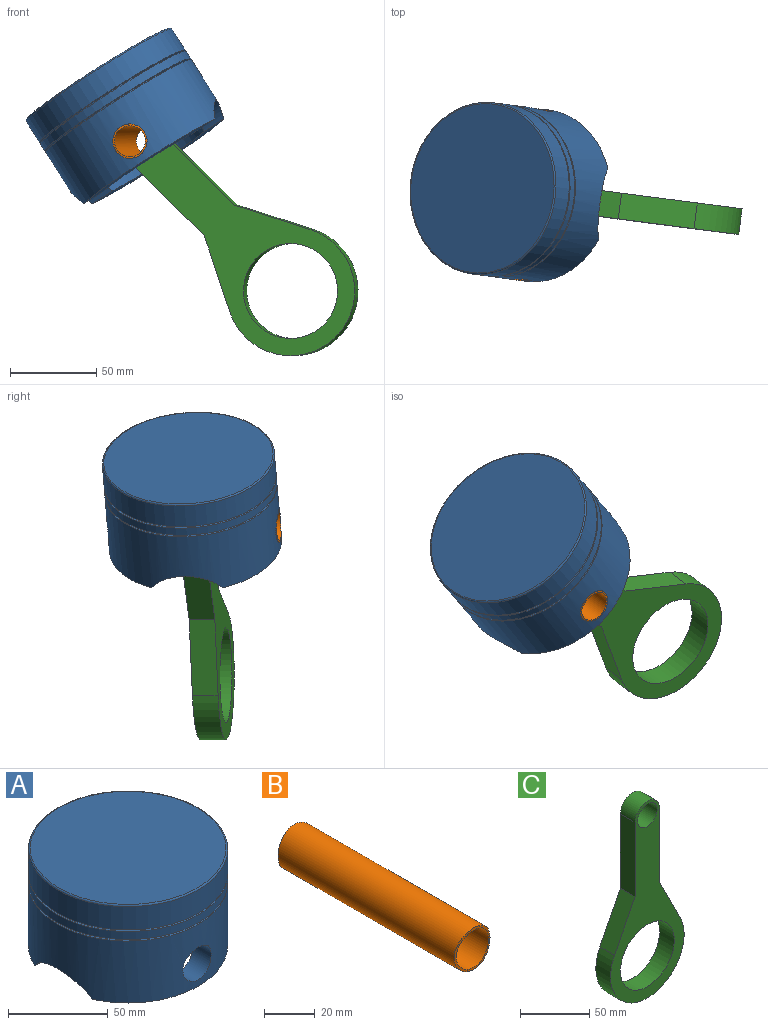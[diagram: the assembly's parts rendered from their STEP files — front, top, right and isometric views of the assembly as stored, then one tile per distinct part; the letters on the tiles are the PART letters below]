
ASSEMBLY  parts=3 mates=2
PART A: 21 faces, bbox 108.2x108.2x60 mm
  f0: plane 91.18x29.47mm, normal (0,0,-1), area 1174.4mm2, adj f10,f12,f17,f18
  f1: plane 98.36x98.36mm, normal (0,0,1), area 7598.2mm2, adj f20
  f2: cylinder r=50mm len=100mm, axis (0,0,-1), area 4498.8mm2, adj f3,f20
  f3: plane 100x100mm, normal (0,0,-1), area 1742.2mm2, adj f2,f4
  f4: cylinder r=44.11mm len=88.21mm, axis (0,0,-1), area 261.3mm2, adj f3,f5
  f5: plane 100x100mm, normal (0,0,1), area 1742.2mm2, adj f4,f6
  f6: cylinder r=50mm len=100mm, axis (0,0,-1), area 1550.4mm2, adj f5,f7
  f7: plane 100x100mm, normal (0,0,-1), area 1742.2mm2, adj f6,f8
  f8: cylinder r=44.11mm len=88.21mm, axis (0,0,-1), area 261.3mm2, adj f7,f9
  f9: plane 100x100mm, normal (0,0,1), area 1742.2mm2, adj f8,f10
  f10: cylinder r=50mm len=100mm, axis (0,0,-1), area 10688.4mm2, adj f0,f9,f11,f14,f15,f16,f17,f18
  f11: plane 91.18x29.47mm, normal (0,0,-1), area 1174.4mm2, adj f10,f12,f16,f19
  f12: cylinder r=37.62mm len=75.24mm, axis (0,0,-1), area 9955mm2, adj f0,f11,f13,f14,f15,f16,f17,f18
  f13: plane 75.24x75.24mm, normal (0,0,-1), area 4446.1mm2, adj f12
  f14: cylinder r=10mm len=20mm, axis (0,-1,0), area 788.7mm2, adj f10,f12
  f15: cylinder r=10mm len=20mm, axis (0,-1,0), area 788.5mm2, adj f10,f12
  f16: cylinder r=25.38mm len=20.53mm, axis (1,0,0), area 312.2mm2, adj f10,f11,f12,f17
  f17: cylinder r=25.38mm len=20.53mm, axis (1,0,0), area 312.2mm2, adj f0,f10,f12,f16
  f18: cylinder r=25.38mm len=20.53mm, axis (1,0,0), area 312.2mm2, adj f0,f10,f12,f19
  f19: cylinder r=25.38mm len=20.53mm, axis (1,0,0), area 312.2mm2, adj f10,f11,f12,f18
  f20: torus R=49.18mm, axis (0,0,-1), area 402.6mm2, adj f1,f2
PART B: 7 faces, bbox 20x99.9x20 mm
  f0: plane 6.99x1.71mm, normal (0,-1,0), area 7.2mm2, adj f1,f2,f4,f5
  f1: cylinder r=9mm len=99.88mm, axis (0,1,0), area 5607.7mm2, adj f0,f3,f4,f5,f6
  f2: cylinder r=10mm len=99.88mm, axis (0,1,0), area 6218.8mm2, adj f0,f3,f4,f5,f6
  f3: plane 6.99x1.71mm, normal (0,-1,0), area 7.2mm2, adj f1,f2,f4,f5
  f4: cylinder r=50mm len=18.74mm, axis (0,0,-1), area 23mm2, adj f0,f1,f2,f3
  f5: cylinder r=50mm len=18.74mm, axis (0,0,-1), area 23mm2, adj f0,f1,f2,f3
  f6: cylinder r=50mm len=20mm, axis (0,0,-1), area 60.2mm2, adj f1,f2
PART C: 10 faces, bbox 75x15x173.9 mm
  f0: cylinder r=12.5mm len=25mm, axis (0,1,0), area 589mm2, adj f1,f5,f8,f9
  f1: plane 65.55x15mm, normal (-1,0,0), area 983.3mm2, adj f0,f2,f8,f9
  f2: plane 41.4x20.96mm, normal (-0.89,0,0.45), area 696.1mm2, adj f1,f3,f8,f9
  f3: cylinder r=37.5mm len=75mm, axis (0,1,0), area 2294.3mm2, adj f2,f4,f8,f9
  f4: plane 41.4x20.96mm, normal (0.89,0,0.45), area 696.1mm2, adj f3,f5,f8,f9
  f5: plane 65.55x15mm, normal (1,0,0), area 983.3mm2, adj f0,f4,f8,f9
  f6: cylinder r=10mm len=20mm, axis (0,1,0), area 942.5mm2, adj f8,f9
  f7: cylinder r=27.5mm len=55mm, axis (0,1,0), area 2591.8mm2, adj f8,f9
  f8: plane 173.89x75mm, normal (0,-1,0), area 4531.6mm2, adj f0,f1,f2,f3,f4,f5,f6,f7
  f9: plane 173.89x75mm, normal (0,1,0), area 4531.6mm2, adj f0,f1,f2,f3,f4,f5,f6,f7
PLACE A rot(axis=(-0.28,0.02,0.96),173deg) t=(-153.11,-41.99,-285.9)mm
PLACE B rot(axis=(0.06,1,-0.01),157.4deg) t=(-154.19,8.47,-274.15)mm
PLACE C rot(axis=(-0.39,0.02,0.92),173.2deg) t=(-161.51,-48.32,-274.15)mm
MATE revolute B.f2 <-> C.f6  axis (0.13,0.99,0) through (-160.55,-40.88,-274.15)mm
MATE revolute B.f2 <-> A.f14  axis (0.13,0.99,0) through (-166.97,-90.71,-274.15)mm
